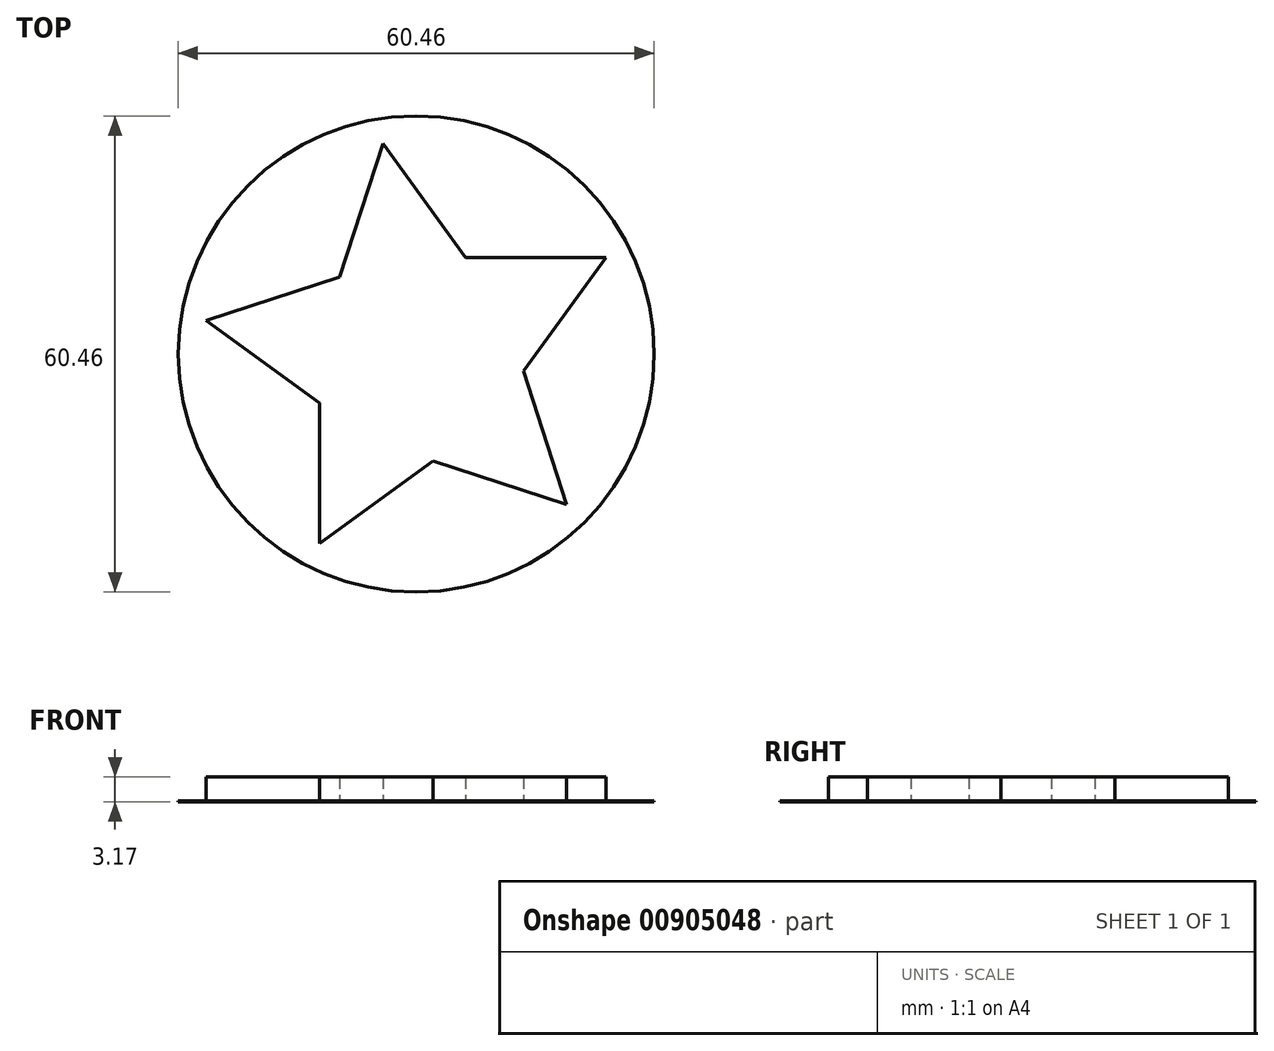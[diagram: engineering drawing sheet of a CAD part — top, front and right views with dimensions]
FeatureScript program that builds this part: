
annotation { "Feature Type Name" : "Feature", "Feature Type Description" : "" }
export const myFeature = defineFeature(function(context is Context, id is Id, definition is map)
    precondition{}
    {
        {
            var Q0;
            Q0=qCreatedBy(makeId("Top.planeOp"),FACE);
            var sketch = newSketch(context, id + "F0", { "sketchPlane" : qUnion([Q0])});
            skCircle(sketch, "E0.cCircle", {"center": v(0, 0) * mm, "radius": 11.15 * mm, "construction": true});
            skLineSegment(sketch, "E0.0", {"start": v(6.25, 12.28) * mm, "end": v(13.6, -2.16) * mm, "construction": true});
            skLineSegment(sketch, "E0.1", {"start": v(13.6, -2.16) * mm, "end": v(2.16, -13.6) * mm, "construction": true});
            skLineSegment(sketch, "E0.2", {"start": v(2.16, -13.6) * mm, "end": v(-12.28, -6.25) * mm, "construction": true});
            skLineSegment(sketch, "E0.3", {"start": v(-12.28, -6.25) * mm, "end": v(-9.74, 9.74) * mm, "construction": true});
            skLineSegment(sketch, "E0.4", {"start": v(-9.74, 9.74) * mm, "end": v(6.25, 12.28) * mm, "construction": true});
            skPoint(sketch, "E0.0.midPoint", {"position": v(9.93, 5.06) * mm});
            skLineSegment(sketch, "E1", {"start": v(-9.74, 9.74) * mm, "end": v(-4.23, 26.7) * mm});
            skLineSegment(sketch, "E2", {"start": v(-4.23, 26.7) * mm, "end": v(6.25, 12.28) * mm});
            skLineSegment(sketch, "E3", {"start": v(6.25, 12.28) * mm, "end": v(24.1, 12.28) * mm});
            skLineSegment(sketch, "E4", {"start": v(24.1, 12.28) * mm, "end": v(13.6, -2.16) * mm});
            skLineSegment(sketch, "E5", {"start": v(13.6, -2.16) * mm, "end": v(19.12, -19.12) * mm});
            skLineSegment(sketch, "E6", {"start": v(19.12, -19.12) * mm, "end": v(2.16, -13.6) * mm});
            skLineSegment(sketch, "E7", {"start": v(-12.28, -6.25) * mm, "end": v(-12.28, -24.1) * mm});
            skLineSegment(sketch, "E8", {"start": v(-12.28, -24.1) * mm, "end": v(2.16, -13.6) * mm});
            skLineSegment(sketch, "E9", {"start": v(-12.28, -6.25) * mm, "end": v(-26.7, 4.23) * mm});
            skLineSegment(sketch, "E10", {"start": v(-26.7, 4.23) * mm, "end": v(-9.74, 9.74) * mm});
            skSolve(sketch);
        }
        {
            var Q0;
            Q0 = qSketchRegion(id + "F0", true);
            extrude(context, id + "F1", {"entities" : qUnion([Q0]), "depth" : 3.17 * mm, "offsetDistance" : 25.4 * mm});
        }
        {
            var Q0;
            Q0=qCreatedBy(makeId("Top.planeOp"),FACE);
            var sketch = newSketch(context, id + "F2", { "sketchPlane" : qUnion([Q0])});
            skCircle(sketch, "E11", {"center": v(0, 0) * mm, "radius": 30.23 * mm});
            skSolve(sketch);
        }
        {
            var Q0;
            Q0 = qSketchRegion(id + "F2", true);
            extrude(context, id + "F3", {"entities" : qUnion([Q0]), "operationType" : NewBodyOperationType.ADD, "depth" : 0.1 * mm, "offsetDistance" : 25.4 * mm});
        }
    });
